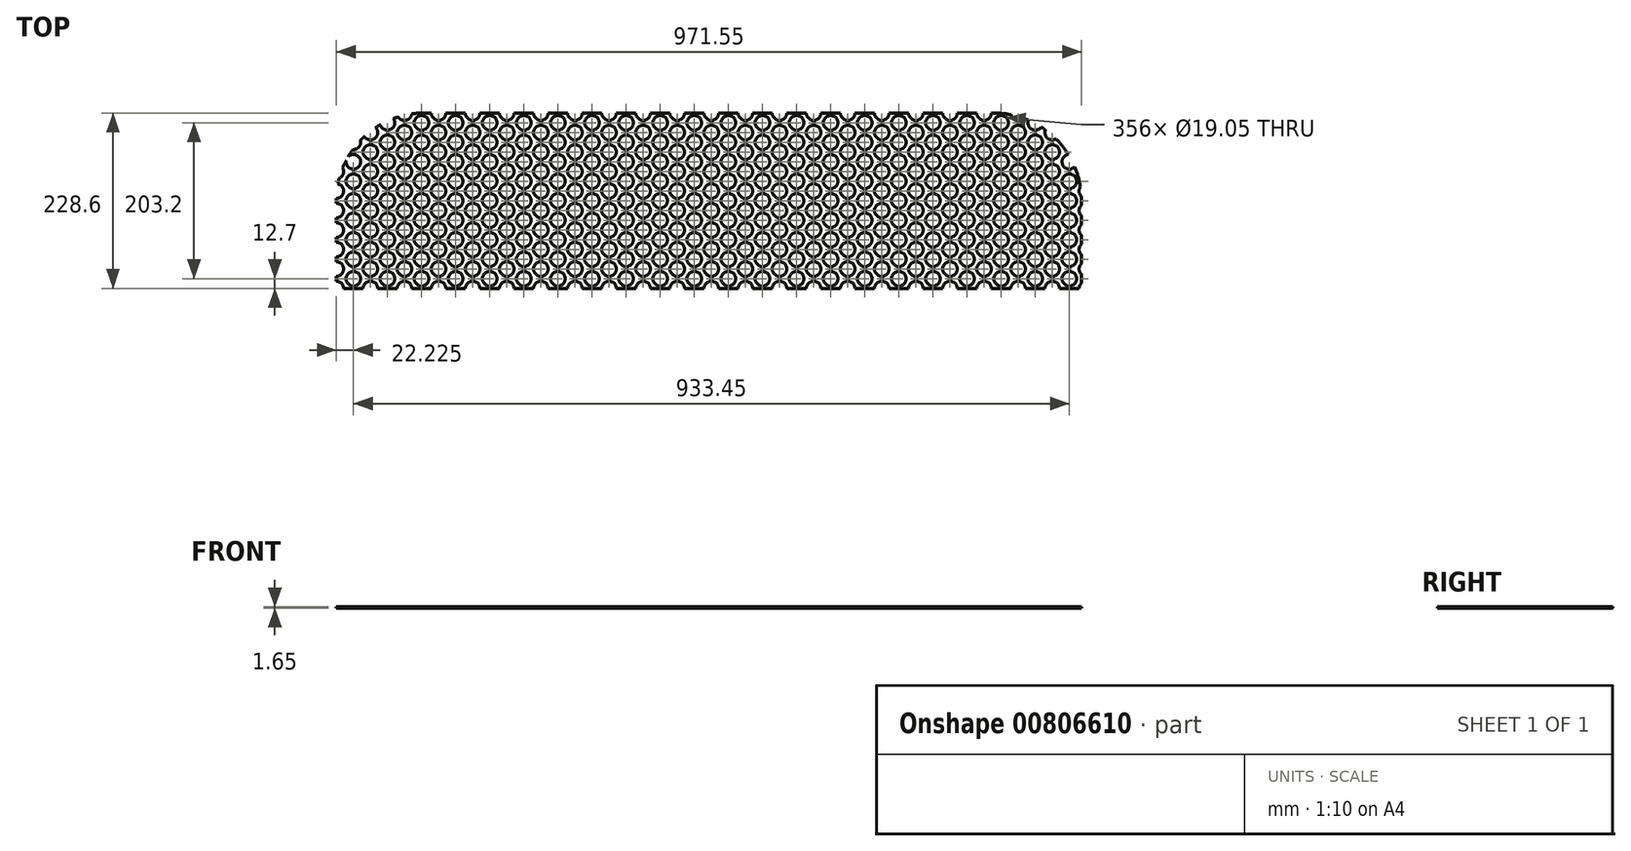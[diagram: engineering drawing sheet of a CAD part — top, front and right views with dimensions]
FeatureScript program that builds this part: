
annotation { "Feature Type Name" : "Feature", "Feature Type Description" : "" }
export const myFeature = defineFeature(function(context is Context, id is Id, definition is map)
    precondition{}
    {
        {
            var Q0;
            Q0=qCreatedBy(makeId("Top.planeOp"),FACE);
            var sketch = newSketch(context, id + "F0", { "sketchPlane" : qUnion([Q0])});
            skArc(sketch, "E0", {"start": v(9.53, 0) * mm, "mid": v(6.74, 6.74) * mm, "end": v(0, 9.53) * mm});
            skArc(sketch, "E1.0.1.0", {"start": v(0, 15.88) * mm, "mid": v(9.53, 25.4) * mm, "end": v(0, 34.92) * mm});
            skArc(sketch, "E1.0.2.0", {"start": v(0, 41.27) * mm, "mid": v(9.53, 50.8) * mm, "end": v(0, 60.32) * mm});
            skArc(sketch, "E1.0.3.0", {"start": v(0, 66.67) * mm, "mid": v(9.53, 76.2) * mm, "end": v(0, 85.72) * mm});
            skArc(sketch, "E1.0.4.0", {"start": v(0, 92.07) * mm, "mid": v(9.53, 101.6) * mm, "end": v(0, 111.12) * mm});
            skArc(sketch, "E1.0.5.0", {"start": v(0.04, 117.48) * mm, "mid": v(9.47, 125.95) * mm, "end": v(2.13, 136.28) * mm});
            skArc(sketch, "E1.0.6.0", {"start": v(3.84, 143.68) * mm, "mid": v(9.04, 149.39) * mm, "end": v(8.3, 157.07) * mm});
            skArc(sketch, "E1.1.0.0", {"start": v(53.98, 0) * mm, "mid": v(44.45, 9.53) * mm, "end": v(34.93, 0) * mm});
            skCircle(sketch, "E1.1.1.0", {"center": v(44.45, 25.4) * mm, "radius": 9.53 * mm});
            skCircle(sketch, "E1.1.2.0", {"center": v(44.45, 50.8) * mm, "radius": 9.53 * mm});
            skCircle(sketch, "E1.1.3.0", {"center": v(44.45, 76.2) * mm, "radius": 9.53 * mm});
            skCircle(sketch, "E1.1.4.0", {"center": v(44.45, 101.6) * mm, "radius": 9.53 * mm});
            skCircle(sketch, "E1.1.5.0", {"center": v(44.45, 127) * mm, "radius": 9.53 * mm});
            skCircle(sketch, "E1.1.6.0", {"center": v(44.45, 152.4) * mm, "radius": 9.53 * mm});
            skCircle(sketch, "E1.1.7.0", {"center": v(44.45, 177.8) * mm, "radius": 9.53 * mm});
            skArc(sketch, "E1.1.8.0", {"start": v(36.47, 198) * mm, "mid": v(50.33, 195.71) * mm, "end": v(51.39, 209.73) * mm});
            skArc(sketch, "E1.2.0.0", {"start": v(98.43, 0) * mm, "mid": v(88.9, 9.53) * mm, "end": v(79.38, 0) * mm});
            skCircle(sketch, "E1.2.1.0", {"center": v(88.9, 25.4) * mm, "radius": 9.53 * mm});
            skCircle(sketch, "E1.2.2.0", {"center": v(88.9, 50.8) * mm, "radius": 9.53 * mm});
            skCircle(sketch, "E1.2.3.0", {"center": v(88.9, 76.2) * mm, "radius": 9.53 * mm});
            skCircle(sketch, "E1.2.4.0", {"center": v(88.9, 101.6) * mm, "radius": 9.53 * mm});
            skCircle(sketch, "E1.2.5.0", {"center": v(88.9, 127) * mm, "radius": 9.53 * mm});
            skCircle(sketch, "E1.2.6.0", {"center": v(88.9, 152.4) * mm, "radius": 9.53 * mm});
            skCircle(sketch, "E1.2.7.0", {"center": v(88.9, 177.8) * mm, "radius": 9.53 * mm});
            skCircle(sketch, "E1.2.8.0", {"center": v(88.9, 203.2) * mm, "radius": 9.53 * mm});
            skArc(sketch, "E1.2.9.0", {"start": v(80.8, 223.58) * mm, "mid": v(90.97, 219.3) * mm, "end": v(98.36, 227.48) * mm});
            skArc(sketch, "E1.3.0.0", {"start": v(142.88, 0) * mm, "mid": v(133.35, 9.53) * mm, "end": v(123.83, 0) * mm});
            skCircle(sketch, "E1.3.1.0", {"center": v(133.35, 25.4) * mm, "radius": 9.53 * mm});
            skCircle(sketch, "E1.3.2.0", {"center": v(133.35, 50.8) * mm, "radius": 9.53 * mm});
            skCircle(sketch, "E1.3.3.0", {"center": v(133.35, 76.2) * mm, "radius": 9.53 * mm});
            skCircle(sketch, "E1.3.4.0", {"center": v(133.35, 101.6) * mm, "radius": 9.53 * mm});
            skCircle(sketch, "E1.3.5.0", {"center": v(133.35, 127) * mm, "radius": 9.53 * mm});
            skCircle(sketch, "E1.3.6.0", {"center": v(133.35, 152.4) * mm, "radius": 9.53 * mm});
            skCircle(sketch, "E1.3.7.0", {"center": v(133.35, 177.8) * mm, "radius": 9.53 * mm});
            skCircle(sketch, "E1.3.8.0", {"center": v(133.35, 203.2) * mm, "radius": 9.53 * mm});
            skArc(sketch, "E1.3.9.0", {"start": v(123.83, 228.6) * mm, "mid": v(133.35, 219.07) * mm, "end": v(142.88, 228.6) * mm});
            skArc(sketch, "E1.4.0.0", {"start": v(187.33, 0) * mm, "mid": v(177.8, 9.53) * mm, "end": v(168.28, 0) * mm});
            skCircle(sketch, "E1.4.1.0", {"center": v(177.8, 25.4) * mm, "radius": 9.53 * mm});
            skCircle(sketch, "E1.4.2.0", {"center": v(177.8, 50.8) * mm, "radius": 9.53 * mm});
            skCircle(sketch, "E1.4.3.0", {"center": v(177.8, 76.2) * mm, "radius": 9.53 * mm});
            skCircle(sketch, "E1.4.4.0", {"center": v(177.8, 101.6) * mm, "radius": 9.53 * mm});
            skCircle(sketch, "E1.4.5.0", {"center": v(177.8, 127) * mm, "radius": 9.53 * mm});
            skCircle(sketch, "E1.4.6.0", {"center": v(177.8, 152.4) * mm, "radius": 9.53 * mm});
            skCircle(sketch, "E1.4.7.0", {"center": v(177.8, 177.8) * mm, "radius": 9.53 * mm});
            skCircle(sketch, "E1.4.8.0", {"center": v(177.8, 203.2) * mm, "radius": 9.53 * mm});
            skArc(sketch, "E1.4.9.0", {"start": v(168.28, 228.6) * mm, "mid": v(177.8, 219.07) * mm, "end": v(187.33, 228.6) * mm});
            skArc(sketch, "E1.5.0.0", {"start": v(231.78, 0) * mm, "mid": v(222.25, 9.53) * mm, "end": v(212.72, 0) * mm});
            skCircle(sketch, "E1.5.1.0", {"center": v(222.25, 25.4) * mm, "radius": 9.53 * mm});
            skCircle(sketch, "E1.5.2.0", {"center": v(222.25, 50.8) * mm, "radius": 9.53 * mm});
            skCircle(sketch, "E1.5.3.0", {"center": v(222.25, 76.2) * mm, "radius": 9.53 * mm});
            skCircle(sketch, "E1.5.4.0", {"center": v(222.25, 101.6) * mm, "radius": 9.53 * mm});
            skCircle(sketch, "E1.5.5.0", {"center": v(222.25, 127) * mm, "radius": 9.53 * mm});
            skCircle(sketch, "E1.5.6.0", {"center": v(222.25, 152.4) * mm, "radius": 9.53 * mm});
            skCircle(sketch, "E1.5.7.0", {"center": v(222.25, 177.8) * mm, "radius": 9.53 * mm});
            skCircle(sketch, "E1.5.8.0", {"center": v(222.25, 203.2) * mm, "radius": 9.53 * mm});
            skArc(sketch, "E1.5.9.0", {"start": v(212.72, 228.6) * mm, "mid": v(222.25, 219.07) * mm, "end": v(231.78, 228.6) * mm});
            skArc(sketch, "E1.6.0.0", {"start": v(276.23, 0) * mm, "mid": v(266.7, 9.53) * mm, "end": v(257.18, 0) * mm});
            skCircle(sketch, "E1.6.1.0", {"center": v(266.7, 25.4) * mm, "radius": 9.53 * mm});
            skCircle(sketch, "E1.6.2.0", {"center": v(266.7, 50.8) * mm, "radius": 9.53 * mm});
            skCircle(sketch, "E1.6.3.0", {"center": v(266.7, 76.2) * mm, "radius": 9.53 * mm});
            skCircle(sketch, "E1.6.4.0", {"center": v(266.7, 101.6) * mm, "radius": 9.53 * mm});
            skCircle(sketch, "E1.6.5.0", {"center": v(266.7, 127) * mm, "radius": 9.53 * mm});
            skCircle(sketch, "E1.6.6.0", {"center": v(266.7, 152.4) * mm, "radius": 9.53 * mm});
            skCircle(sketch, "E1.6.7.0", {"center": v(266.7, 177.8) * mm, "radius": 9.53 * mm});
            skCircle(sketch, "E1.6.8.0", {"center": v(266.7, 203.2) * mm, "radius": 9.53 * mm});
            skArc(sketch, "E1.6.9.0", {"start": v(257.18, 228.6) * mm, "mid": v(266.7, 219.07) * mm, "end": v(276.23, 228.6) * mm});
            skArc(sketch, "E1.7.0.0", {"start": v(320.68, 0) * mm, "mid": v(311.15, 9.53) * mm, "end": v(301.63, 0) * mm});
            skCircle(sketch, "E1.7.1.0", {"center": v(311.15, 25.4) * mm, "radius": 9.53 * mm});
            skCircle(sketch, "E1.7.2.0", {"center": v(311.15, 50.8) * mm, "radius": 9.53 * mm});
            skCircle(sketch, "E1.7.3.0", {"center": v(311.15, 76.2) * mm, "radius": 9.53 * mm});
            skCircle(sketch, "E1.7.4.0", {"center": v(311.15, 101.6) * mm, "radius": 9.53 * mm});
            skCircle(sketch, "E1.7.5.0", {"center": v(311.15, 127) * mm, "radius": 9.53 * mm});
            skCircle(sketch, "E1.7.6.0", {"center": v(311.15, 152.4) * mm, "radius": 9.53 * mm});
            skCircle(sketch, "E1.7.7.0", {"center": v(311.15, 177.8) * mm, "radius": 9.53 * mm});
            skCircle(sketch, "E1.7.8.0", {"center": v(311.15, 203.2) * mm, "radius": 9.53 * mm});
            skArc(sketch, "E1.7.9.0", {"start": v(301.63, 228.6) * mm, "mid": v(311.15, 219.07) * mm, "end": v(320.68, 228.6) * mm});
            skArc(sketch, "E1.8.0.0", {"start": v(365.13, 0) * mm, "mid": v(355.6, 9.53) * mm, "end": v(346.08, 0) * mm});
            skCircle(sketch, "E1.8.1.0", {"center": v(355.6, 25.4) * mm, "radius": 9.53 * mm});
            skCircle(sketch, "E1.8.2.0", {"center": v(355.6, 50.8) * mm, "radius": 9.53 * mm});
            skCircle(sketch, "E1.8.3.0", {"center": v(355.6, 76.2) * mm, "radius": 9.53 * mm});
            skCircle(sketch, "E1.8.4.0", {"center": v(355.6, 101.6) * mm, "radius": 9.53 * mm});
            skCircle(sketch, "E1.8.5.0", {"center": v(355.6, 127) * mm, "radius": 9.53 * mm});
            skCircle(sketch, "E1.8.6.0", {"center": v(355.6, 152.4) * mm, "radius": 9.53 * mm});
            skCircle(sketch, "E1.8.7.0", {"center": v(355.6, 177.8) * mm, "radius": 9.53 * mm});
            skCircle(sketch, "E1.8.8.0", {"center": v(355.6, 203.2) * mm, "radius": 9.53 * mm});
            skArc(sketch, "E1.8.9.0", {"start": v(346.08, 228.6) * mm, "mid": v(355.6, 219.07) * mm, "end": v(365.13, 228.6) * mm});
            skArc(sketch, "E1.9.0.0", {"start": v(409.58, 0) * mm, "mid": v(400.05, 9.53) * mm, "end": v(390.53, 0) * mm});
            skCircle(sketch, "E1.9.1.0", {"center": v(400.05, 25.4) * mm, "radius": 9.53 * mm});
            skCircle(sketch, "E1.9.2.0", {"center": v(400.05, 50.8) * mm, "radius": 9.53 * mm});
            skCircle(sketch, "E1.9.3.0", {"center": v(400.05, 76.2) * mm, "radius": 9.53 * mm});
            skCircle(sketch, "E1.9.4.0", {"center": v(400.05, 101.6) * mm, "radius": 9.53 * mm});
            skCircle(sketch, "E1.9.5.0", {"center": v(400.05, 127) * mm, "radius": 9.53 * mm});
            skCircle(sketch, "E1.9.6.0", {"center": v(400.05, 152.4) * mm, "radius": 9.53 * mm});
            skCircle(sketch, "E1.9.7.0", {"center": v(400.05, 177.8) * mm, "radius": 9.53 * mm});
            skCircle(sketch, "E1.9.8.0", {"center": v(400.05, 203.2) * mm, "radius": 9.53 * mm});
            skArc(sketch, "E1.9.9.0", {"start": v(390.53, 228.6) * mm, "mid": v(400.05, 219.07) * mm, "end": v(409.58, 228.6) * mm});
            skArc(sketch, "E1.10.0.0", {"start": v(454.03, 0) * mm, "mid": v(444.5, 9.53) * mm, "end": v(434.98, 0) * mm});
            skCircle(sketch, "E1.10.1.0", {"center": v(444.5, 25.4) * mm, "radius": 9.53 * mm});
            skCircle(sketch, "E1.10.2.0", {"center": v(444.5, 50.8) * mm, "radius": 9.53 * mm});
            skCircle(sketch, "E1.10.3.0", {"center": v(444.5, 76.2) * mm, "radius": 9.53 * mm});
            skCircle(sketch, "E1.10.4.0", {"center": v(444.5, 101.6) * mm, "radius": 9.53 * mm});
            skCircle(sketch, "E1.10.5.0", {"center": v(444.5, 127) * mm, "radius": 9.53 * mm});
            skCircle(sketch, "E1.10.6.0", {"center": v(444.5, 152.4) * mm, "radius": 9.53 * mm});
            skCircle(sketch, "E1.10.7.0", {"center": v(444.5, 177.8) * mm, "radius": 9.53 * mm});
            skCircle(sketch, "E1.10.8.0", {"center": v(444.5, 203.2) * mm, "radius": 9.53 * mm});
            skArc(sketch, "E1.10.9.0", {"start": v(434.98, 228.6) * mm, "mid": v(444.5, 219.07) * mm, "end": v(454.03, 228.6) * mm});
            skArc(sketch, "E1.11.0.0", {"start": v(498.48, 0) * mm, "mid": v(488.95, 9.53) * mm, "end": v(479.43, 0) * mm});
            skCircle(sketch, "E1.11.1.0", {"center": v(488.95, 25.4) * mm, "radius": 9.53 * mm});
            skCircle(sketch, "E1.11.2.0", {"center": v(488.95, 50.8) * mm, "radius": 9.53 * mm});
            skCircle(sketch, "E1.11.3.0", {"center": v(488.95, 76.2) * mm, "radius": 9.53 * mm});
            skCircle(sketch, "E1.11.4.0", {"center": v(488.95, 101.6) * mm, "radius": 9.53 * mm});
            skCircle(sketch, "E1.11.5.0", {"center": v(488.95, 127) * mm, "radius": 9.53 * mm});
            skCircle(sketch, "E1.11.6.0", {"center": v(488.95, 152.4) * mm, "radius": 9.53 * mm});
            skCircle(sketch, "E1.11.7.0", {"center": v(488.95, 177.8) * mm, "radius": 9.53 * mm});
            skCircle(sketch, "E1.11.8.0", {"center": v(488.95, 203.2) * mm, "radius": 9.53 * mm});
            skArc(sketch, "E1.11.9.0", {"start": v(479.43, 228.6) * mm, "mid": v(488.95, 219.07) * mm, "end": v(498.48, 228.6) * mm});
            skArc(sketch, "E1.12.0.0", {"start": v(542.93, 0) * mm, "mid": v(533.4, 9.53) * mm, "end": v(523.88, 0) * mm});
            skCircle(sketch, "E1.12.1.0", {"center": v(533.4, 25.4) * mm, "radius": 9.53 * mm});
            skCircle(sketch, "E1.12.2.0", {"center": v(533.4, 50.8) * mm, "radius": 9.53 * mm});
            skCircle(sketch, "E1.12.3.0", {"center": v(533.4, 76.2) * mm, "radius": 9.53 * mm});
            skCircle(sketch, "E1.12.4.0", {"center": v(533.4, 101.6) * mm, "radius": 9.53 * mm});
            skCircle(sketch, "E1.12.5.0", {"center": v(533.4, 127) * mm, "radius": 9.53 * mm});
            skCircle(sketch, "E1.12.6.0", {"center": v(533.4, 152.4) * mm, "radius": 9.53 * mm});
            skCircle(sketch, "E1.12.7.0", {"center": v(533.4, 177.8) * mm, "radius": 9.53 * mm});
            skCircle(sketch, "E1.12.8.0", {"center": v(533.4, 203.2) * mm, "radius": 9.53 * mm});
            skArc(sketch, "E1.12.9.0", {"start": v(523.88, 228.6) * mm, "mid": v(533.4, 219.07) * mm, "end": v(542.93, 228.6) * mm});
            skArc(sketch, "E1.13.0.0", {"start": v(587.38, 0) * mm, "mid": v(577.85, 9.53) * mm, "end": v(568.33, 0) * mm});
            skCircle(sketch, "E1.13.1.0", {"center": v(577.85, 25.4) * mm, "radius": 9.53 * mm});
            skCircle(sketch, "E1.13.2.0", {"center": v(577.85, 50.8) * mm, "radius": 9.53 * mm});
            skCircle(sketch, "E1.13.3.0", {"center": v(577.85, 76.2) * mm, "radius": 9.53 * mm});
            skCircle(sketch, "E1.13.4.0", {"center": v(577.85, 101.6) * mm, "radius": 9.53 * mm});
            skCircle(sketch, "E1.13.5.0", {"center": v(577.85, 127) * mm, "radius": 9.53 * mm});
            skCircle(sketch, "E1.13.6.0", {"center": v(577.85, 152.4) * mm, "radius": 9.53 * mm});
            skCircle(sketch, "E1.13.7.0", {"center": v(577.85, 177.8) * mm, "radius": 9.53 * mm});
            skCircle(sketch, "E1.13.8.0", {"center": v(577.85, 203.2) * mm, "radius": 9.53 * mm});
            skArc(sketch, "E1.13.9.0", {"start": v(568.33, 228.6) * mm, "mid": v(577.85, 219.07) * mm, "end": v(587.38, 228.6) * mm});
            skArc(sketch, "E1.14.0.0", {"start": v(631.83, 0) * mm, "mid": v(622.3, 9.53) * mm, "end": v(612.78, 0) * mm});
            skCircle(sketch, "E1.14.1.0", {"center": v(622.3, 25.4) * mm, "radius": 9.53 * mm});
            skCircle(sketch, "E1.14.2.0", {"center": v(622.3, 50.8) * mm, "radius": 9.53 * mm});
            skCircle(sketch, "E1.14.3.0", {"center": v(622.3, 76.2) * mm, "radius": 9.53 * mm});
            skCircle(sketch, "E1.14.4.0", {"center": v(622.3, 101.6) * mm, "radius": 9.53 * mm});
            skCircle(sketch, "E1.14.5.0", {"center": v(622.3, 127) * mm, "radius": 9.53 * mm});
            skCircle(sketch, "E1.14.6.0", {"center": v(622.3, 152.4) * mm, "radius": 9.53 * mm});
            skCircle(sketch, "E1.14.7.0", {"center": v(622.3, 177.8) * mm, "radius": 9.53 * mm});
            skCircle(sketch, "E1.14.8.0", {"center": v(622.3, 203.2) * mm, "radius": 9.53 * mm});
            skArc(sketch, "E1.14.9.0", {"start": v(612.78, 228.6) * mm, "mid": v(622.3, 219.07) * mm, "end": v(631.83, 228.6) * mm});
            skArc(sketch, "E1.15.0.0", {"start": v(676.28, 0) * mm, "mid": v(666.75, 9.53) * mm, "end": v(657.23, 0) * mm});
            skCircle(sketch, "E1.15.1.0", {"center": v(666.75, 25.4) * mm, "radius": 9.53 * mm});
            skCircle(sketch, "E1.15.2.0", {"center": v(666.75, 50.8) * mm, "radius": 9.53 * mm});
            skCircle(sketch, "E1.15.3.0", {"center": v(666.75, 76.2) * mm, "radius": 9.53 * mm});
            skCircle(sketch, "E1.15.4.0", {"center": v(666.75, 101.6) * mm, "radius": 9.53 * mm});
            skCircle(sketch, "E1.15.5.0", {"center": v(666.75, 127) * mm, "radius": 9.53 * mm});
            skCircle(sketch, "E1.15.6.0", {"center": v(666.75, 152.4) * mm, "radius": 9.53 * mm});
            skCircle(sketch, "E1.15.7.0", {"center": v(666.75, 177.8) * mm, "radius": 9.53 * mm});
            skCircle(sketch, "E1.15.8.0", {"center": v(666.75, 203.2) * mm, "radius": 9.53 * mm});
            skArc(sketch, "E1.15.9.0", {"start": v(657.23, 228.6) * mm, "mid": v(666.75, 219.07) * mm, "end": v(676.28, 228.6) * mm});
            skArc(sketch, "E1.16.0.0", {"start": v(720.73, 0) * mm, "mid": v(711.2, 9.53) * mm, "end": v(701.68, 0) * mm});
            skCircle(sketch, "E1.16.1.0", {"center": v(711.2, 25.4) * mm, "radius": 9.53 * mm});
            skCircle(sketch, "E1.16.2.0", {"center": v(711.2, 50.8) * mm, "radius": 9.53 * mm});
            skCircle(sketch, "E1.16.3.0", {"center": v(711.2, 76.2) * mm, "radius": 9.53 * mm});
            skCircle(sketch, "E1.16.4.0", {"center": v(711.2, 101.6) * mm, "radius": 9.53 * mm});
            skCircle(sketch, "E1.16.5.0", {"center": v(711.2, 127) * mm, "radius": 9.53 * mm});
            skCircle(sketch, "E1.16.6.0", {"center": v(711.2, 152.4) * mm, "radius": 9.53 * mm});
            skCircle(sketch, "E1.16.7.0", {"center": v(711.2, 177.8) * mm, "radius": 9.53 * mm});
            skCircle(sketch, "E1.16.8.0", {"center": v(711.2, 203.2) * mm, "radius": 9.53 * mm});
            skArc(sketch, "E1.16.9.0", {"start": v(701.68, 228.6) * mm, "mid": v(711.2, 219.07) * mm, "end": v(720.73, 228.6) * mm});
            skArc(sketch, "E1.17.0.0", {"start": v(765.18, 0) * mm, "mid": v(755.65, 9.53) * mm, "end": v(746.12, 0) * mm});
            skCircle(sketch, "E1.17.1.0", {"center": v(755.65, 25.4) * mm, "radius": 9.53 * mm});
            skCircle(sketch, "E1.17.2.0", {"center": v(755.65, 50.8) * mm, "radius": 9.53 * mm});
            skCircle(sketch, "E1.17.3.0", {"center": v(755.65, 76.2) * mm, "radius": 9.53 * mm});
            skCircle(sketch, "E1.17.4.0", {"center": v(755.65, 101.6) * mm, "radius": 9.53 * mm});
            skCircle(sketch, "E1.17.5.0", {"center": v(755.65, 127) * mm, "radius": 9.53 * mm});
            skCircle(sketch, "E1.17.6.0", {"center": v(755.65, 152.4) * mm, "radius": 9.53 * mm});
            skCircle(sketch, "E1.17.7.0", {"center": v(755.65, 177.8) * mm, "radius": 9.53 * mm});
            skCircle(sketch, "E1.17.8.0", {"center": v(755.65, 203.2) * mm, "radius": 9.53 * mm});
            skArc(sketch, "E1.17.9.0", {"start": v(746.12, 228.6) * mm, "mid": v(755.65, 219.07) * mm, "end": v(765.18, 228.6) * mm});
            skArc(sketch, "E1.18.0.0", {"start": v(809.62, 0) * mm, "mid": v(800.1, 9.53) * mm, "end": v(790.58, 0) * mm});
            skCircle(sketch, "E1.18.1.0", {"center": v(800.1, 25.4) * mm, "radius": 9.53 * mm});
            skCircle(sketch, "E1.18.2.0", {"center": v(800.1, 50.8) * mm, "radius": 9.53 * mm});
            skCircle(sketch, "E1.18.3.0", {"center": v(800.1, 76.2) * mm, "radius": 9.53 * mm});
            skCircle(sketch, "E1.18.4.0", {"center": v(800.1, 101.6) * mm, "radius": 9.53 * mm});
            skCircle(sketch, "E1.18.5.0", {"center": v(800.1, 127) * mm, "radius": 9.53 * mm});
            skCircle(sketch, "E1.18.6.0", {"center": v(800.1, 152.4) * mm, "radius": 9.53 * mm});
            skCircle(sketch, "E1.18.7.0", {"center": v(800.1, 177.8) * mm, "radius": 9.53 * mm});
            skCircle(sketch, "E1.18.8.0", {"center": v(800.1, 203.2) * mm, "radius": 9.53 * mm});
            skArc(sketch, "E1.18.9.0", {"start": v(790.58, 228.6) * mm, "mid": v(800.1, 219.07) * mm, "end": v(809.62, 228.6) * mm});
            skArc(sketch, "E1.19.0.0", {"start": v(854.08, 0) * mm, "mid": v(844.55, 9.53) * mm, "end": v(835.02, 0) * mm});
            skCircle(sketch, "E1.19.1.0", {"center": v(844.55, 25.4) * mm, "radius": 9.53 * mm});
            skCircle(sketch, "E1.19.2.0", {"center": v(844.55, 50.8) * mm, "radius": 9.53 * mm});
            skCircle(sketch, "E1.19.3.0", {"center": v(844.55, 76.2) * mm, "radius": 9.53 * mm});
            skCircle(sketch, "E1.19.4.0", {"center": v(844.55, 101.6) * mm, "radius": 9.53 * mm});
            skCircle(sketch, "E1.19.5.0", {"center": v(844.55, 127) * mm, "radius": 9.53 * mm});
            skCircle(sketch, "E1.19.6.0", {"center": v(844.55, 152.4) * mm, "radius": 9.53 * mm});
            skCircle(sketch, "E1.19.7.0", {"center": v(844.55, 177.8) * mm, "radius": 9.53 * mm});
            skCircle(sketch, "E1.19.8.0", {"center": v(844.55, 203.2) * mm, "radius": 9.53 * mm});
            skArc(sketch, "E1.19.9.0", {"start": v(835.02, 228.6) * mm, "mid": v(844.55, 219.07) * mm, "end": v(854.08, 228.6) * mm});
            skArc(sketch, "E1.20.0.0", {"start": v(898.52, 0) * mm, "mid": v(889, 9.53) * mm, "end": v(879.48, 0) * mm});
            skCircle(sketch, "E1.20.1.0", {"center": v(889, 25.4) * mm, "radius": 9.53 * mm});
            skCircle(sketch, "E1.20.2.0", {"center": v(889, 50.8) * mm, "radius": 9.53 * mm});
            skCircle(sketch, "E1.20.3.0", {"center": v(889, 76.2) * mm, "radius": 9.53 * mm});
            skCircle(sketch, "E1.20.4.0", {"center": v(889, 101.6) * mm, "radius": 9.53 * mm});
            skCircle(sketch, "E1.20.5.0", {"center": v(889, 127) * mm, "radius": 9.53 * mm});
            skCircle(sketch, "E1.20.6.0", {"center": v(889, 152.4) * mm, "radius": 9.53 * mm});
            skCircle(sketch, "E1.20.7.0", {"center": v(889, 177.8) * mm, "radius": 9.53 * mm});
            skCircle(sketch, "E1.20.8.0", {"center": v(889, 203.2) * mm, "radius": 9.53 * mm});
            skArc(sketch, "E1.20.9.0", {"start": v(879.74, 226.37) * mm, "mid": v(886.45, 219.42) * mm, "end": v(895.78, 221.91) * mm});
            skArc(sketch, "E1.21.0.0", {"start": v(942.98, 0) * mm, "mid": v(933.45, 9.53) * mm, "end": v(923.93, 0) * mm});
            skCircle(sketch, "E1.21.1.0", {"center": v(933.45, 25.4) * mm, "radius": 9.53 * mm});
            skCircle(sketch, "E1.21.2.0", {"center": v(933.45, 50.8) * mm, "radius": 9.53 * mm});
            skCircle(sketch, "E1.21.3.0", {"center": v(933.45, 76.2) * mm, "radius": 9.53 * mm});
            skCircle(sketch, "E1.21.4.0", {"center": v(933.45, 101.6) * mm, "radius": 9.53 * mm});
            skCircle(sketch, "E1.21.5.0", {"center": v(933.45, 127) * mm, "radius": 9.53 * mm});
            skCircle(sketch, "E1.21.6.0", {"center": v(933.45, 152.4) * mm, "radius": 9.53 * mm});
            skCircle(sketch, "E1.21.7.0", {"center": v(933.45, 177.8) * mm, "radius": 9.53 * mm});
            skArc(sketch, "E1.21.8.0", {"start": v(924.58, 206.67) * mm, "mid": v(927.25, 195.97) * mm, "end": v(938.23, 194.96) * mm});
            skArc(sketch, "E1.22.0.0", {"start": v(971.55, 7.1) * mm, "mid": v(969.2, 3.89) * mm, "end": v(968.38, 0) * mm});
            skArc(sketch, "E1.22.1.0", {"start": v(971.55, 32.5) * mm, "mid": v(968.38, 25.4) * mm, "end": v(971.55, 18.3) * mm});
            skArc(sketch, "E1.22.2.0", {"start": v(971.55, 57.9) * mm, "mid": v(968.38, 50.8) * mm, "end": v(971.55, 43.7) * mm});
            skArc(sketch, "E1.22.3.0", {"start": v(971.55, 83.3) * mm, "mid": v(968.38, 76.2) * mm, "end": v(971.55, 69.1) * mm});
            skArc(sketch, "E1.22.4.0", {"start": v(971.55, 108.7) * mm, "mid": v(968.38, 101.6) * mm, "end": v(971.55, 94.5) * mm});
            skArc(sketch, "E1.22.5.0", {"start": v(970.1, 132.46) * mm, "mid": v(968.43, 126) * mm, "end": v(971.4, 120.03) * mm});
            skLineSegment(sketch, "E1.direction1", {"start": v(9.53, 0) * mm, "end": v(34.93, 0) * mm, "construction": true});
            skLineSegment(sketch, "E1.direction2", {"start": v(0, 9.53) * mm, "end": v(0, 15.88) * mm, "construction": true});
            skLineSegment(sketch, "E2.bottom", {"start": v(9.53, 0) * mm, "end": v(34.92, 0) * mm});
            skLineSegment(sketch, "E2.left", {"start": v(0, 9.53) * mm, "end": v(0, 25.4) * mm});
            skLineSegment(sketch, "E2.right", {"start": v(971.55, 7.1) * mm, "end": v(971.55, 18.3) * mm});
            skArc(sketch, "E3.filletArc", {"start": v(971.55, 114.3) * mm, "mid": v(971.51, 117.17) * mm, "end": v(971.4, 120.03) * mm});
            skPoint(sketch, "E4.visualSharp", {"position": v(0, 228.6) * mm});
            skArc(sketch, "E4.filletArc", {"start": v(114.3, 228.6) * mm, "mid": v(106.31, 228.32) * mm, "end": v(98.36, 227.48) * mm});
            skArc(sketch, "E5.trimOffspring", {"start": v(3.84, 143.68) * mm, "mid": v(2.93, 140) * mm, "end": v(2.13, 136.28) * mm});
            skArc(sketch, "E6.trimOffspring", {"start": v(0.04, 117.48) * mm, "mid": v(0.01, 115.89) * mm, "end": v(0, 114.3) * mm});
            skLineSegment(sketch, "E7.trimOffspring", {"start": v(0, 111.12) * mm, "end": v(0, 114.3) * mm});
            skLineSegment(sketch, "E8.trimOffspring", {"start": v(0, 85.72) * mm, "end": v(0, 92.07) * mm});
            skArc(sketch, "E9.trimOffspring", {"start": v(924.58, 206.67) * mm, "mid": v(921.84, 208.6) * mm, "end": v(919.04, 210.46) * mm});
            skArc(sketch, "E10.trimOffspring", {"start": v(879.74, 226.37) * mm, "mid": v(868.55, 228.04) * mm, "end": v(857.25, 228.6) * mm});
            skArc(sketch, "E11.trimOffspring", {"start": v(970.1, 132.46) * mm, "mid": v(967.14, 145.75) * mm, "end": v(962.62, 158.58) * mm});
            skLineSegment(sketch, "E12.trimOffspring", {"start": v(971.55, 108.7) * mm, "end": v(971.55, 114.3) * mm});
            skLineSegment(sketch, "E13.trimOffspring", {"start": v(971.55, 83.3) * mm, "end": v(971.55, 94.5) * mm});
            skLineSegment(sketch, "E14.trimOffspring", {"start": v(971.55, 57.9) * mm, "end": v(971.55, 69.1) * mm});
            skLineSegment(sketch, "E15.trimOffspring", {"start": v(971.55, 32.5) * mm, "end": v(971.55, 43.7) * mm});
            skLineSegment(sketch, "E16.trimOffspring", {"start": v(809.62, 0) * mm, "end": v(835.02, 0) * mm});
            skLineSegment(sketch, "E17.trimOffspring", {"start": v(898.52, 0) * mm, "end": v(923.93, 0) * mm});
            skLineSegment(sketch, "E18.trimOffspring", {"start": v(942.98, 0) * mm, "end": v(968.38, 0) * mm});
            skLineSegment(sketch, "E19", {"start": v(854.08, 0) * mm, "end": v(879.48, 0) * mm});
            skLineSegment(sketch, "E20.trimOffspring", {"start": v(765.18, 0) * mm, "end": v(790.58, 0) * mm});
            skLineSegment(sketch, "E21.trimOffspring", {"start": v(720.73, 0) * mm, "end": v(746.12, 0) * mm});
            skLineSegment(sketch, "E22.trimOffspring", {"start": v(676.28, 0) * mm, "end": v(701.68, 0) * mm});
            skLineSegment(sketch, "E23.trimOffspring", {"start": v(631.83, 0) * mm, "end": v(657.23, 0) * mm});
            skLineSegment(sketch, "E24.trimOffspring", {"start": v(276.23, 0) * mm, "end": v(301.63, 0) * mm});
            skLineSegment(sketch, "E25.trimOffspring", {"start": v(320.68, 0) * mm, "end": v(346.08, 0) * mm});
            skLineSegment(sketch, "E26.trimOffspring", {"start": v(365.13, 0) * mm, "end": v(390.53, 0) * mm});
            skLineSegment(sketch, "E27.trimOffspring", {"start": v(409.58, 0) * mm, "end": v(434.98, 0) * mm});
            skLineSegment(sketch, "E28.trimOffspring", {"start": v(454.03, 0) * mm, "end": v(479.43, 0) * mm});
            skLineSegment(sketch, "E29.trimOffspring", {"start": v(498.48, 0) * mm, "end": v(523.88, 0) * mm});
            skLineSegment(sketch, "E30.trimOffspring", {"start": v(542.93, 0) * mm, "end": v(568.33, 0) * mm});
            skLineSegment(sketch, "E31.trimOffspring", {"start": v(587.38, 0) * mm, "end": v(612.78, 0) * mm});
            skLineSegment(sketch, "E32", {"start": v(257.18, 0) * mm, "end": v(231.78, 0) * mm});
            skLineSegment(sketch, "E33.trimOffspring", {"start": v(187.33, 0) * mm, "end": v(212.72, 0) * mm});
            skLineSegment(sketch, "E34.trimOffspring", {"start": v(142.88, 0) * mm, "end": v(168.28, 0) * mm});
            skLineSegment(sketch, "E35.trimOffspring", {"start": v(98.42, 0) * mm, "end": v(123.83, 0) * mm});
            skCircle(sketch, "E36", {"center": v(22.22, 12.7) * mm, "radius": 9.53 * mm});
            skCircle(sketch, "E37.0.1.0", {"center": v(22.22, 38.1) * mm, "radius": 9.53 * mm});
            skCircle(sketch, "E37.0.2.0", {"center": v(22.22, 63.5) * mm, "radius": 9.53 * mm});
            skCircle(sketch, "E37.0.3.0", {"center": v(22.22, 88.9) * mm, "radius": 9.53 * mm});
            skCircle(sketch, "E37.0.4.0", {"center": v(22.22, 114.3) * mm, "radius": 9.53 * mm});
            skCircle(sketch, "E37.0.5.0", {"center": v(22.22, 139.7) * mm, "radius": 9.53 * mm});
            skArc(sketch, "E37.0.6.0", {"start": v(12.9, 167.06) * mm, "mid": v(30.56, 160.5) * mm, "end": v(15.6, 171.94) * mm});
            skArc(sketch, "E37.0.7.0", {"start": v(21.48, 181) * mm, "mid": v(29.56, 184.43) * mm, "end": v(31.41, 193) * mm});
            skCircle(sketch, "E37.1.0.0", {"center": v(66.67, 12.7) * mm, "radius": 9.53 * mm});
            skCircle(sketch, "E37.1.1.0", {"center": v(66.67, 38.1) * mm, "radius": 9.53 * mm});
            skCircle(sketch, "E37.1.2.0", {"center": v(66.67, 63.5) * mm, "radius": 9.53 * mm});
            skCircle(sketch, "E37.1.3.0", {"center": v(66.67, 88.9) * mm, "radius": 9.53 * mm});
            skCircle(sketch, "E37.1.4.0", {"center": v(66.67, 114.3) * mm, "radius": 9.53 * mm});
            skCircle(sketch, "E37.1.5.0", {"center": v(66.67, 139.7) * mm, "radius": 9.53 * mm});
            skCircle(sketch, "E37.1.6.0", {"center": v(66.67, 165.1) * mm, "radius": 9.53 * mm});
            skCircle(sketch, "E37.1.7.0", {"center": v(66.67, 190.5) * mm, "radius": 9.53 * mm});
            skCircle(sketch, "E37.2.0.0", {"center": v(111.12, 12.7) * mm, "radius": 9.53 * mm});
            skCircle(sketch, "E37.2.1.0", {"center": v(111.12, 38.1) * mm, "radius": 9.53 * mm});
            skCircle(sketch, "E37.2.2.0", {"center": v(111.12, 63.5) * mm, "radius": 9.53 * mm});
            skCircle(sketch, "E37.2.3.0", {"center": v(111.12, 88.9) * mm, "radius": 9.53 * mm});
            skCircle(sketch, "E37.2.4.0", {"center": v(111.12, 114.3) * mm, "radius": 9.53 * mm});
            skCircle(sketch, "E37.2.5.0", {"center": v(111.12, 139.7) * mm, "radius": 9.53 * mm});
            skCircle(sketch, "E37.2.6.0", {"center": v(111.12, 165.1) * mm, "radius": 9.53 * mm});
            skCircle(sketch, "E37.2.7.0", {"center": v(111.12, 190.5) * mm, "radius": 9.53 * mm});
            skCircle(sketch, "E37.3.0.0", {"center": v(155.58, 12.7) * mm, "radius": 9.53 * mm});
            skCircle(sketch, "E37.3.1.0", {"center": v(155.58, 38.1) * mm, "radius": 9.53 * mm});
            skCircle(sketch, "E37.3.2.0", {"center": v(155.58, 63.5) * mm, "radius": 9.53 * mm});
            skCircle(sketch, "E37.3.3.0", {"center": v(155.58, 88.9) * mm, "radius": 9.53 * mm});
            skCircle(sketch, "E37.3.4.0", {"center": v(155.58, 114.3) * mm, "radius": 9.53 * mm});
            skCircle(sketch, "E37.3.5.0", {"center": v(155.58, 139.7) * mm, "radius": 9.53 * mm});
            skCircle(sketch, "E37.3.6.0", {"center": v(155.58, 165.1) * mm, "radius": 9.53 * mm});
            skCircle(sketch, "E37.3.7.0", {"center": v(155.58, 190.5) * mm, "radius": 9.53 * mm});
            skCircle(sketch, "E37.4.0.0", {"center": v(200.03, 12.7) * mm, "radius": 9.53 * mm});
            skCircle(sketch, "E37.4.1.0", {"center": v(200.03, 38.1) * mm, "radius": 9.53 * mm});
            skCircle(sketch, "E37.4.2.0", {"center": v(200.03, 63.5) * mm, "radius": 9.53 * mm});
            skCircle(sketch, "E37.4.3.0", {"center": v(200.03, 88.9) * mm, "radius": 9.53 * mm});
            skCircle(sketch, "E37.4.4.0", {"center": v(200.03, 114.3) * mm, "radius": 9.53 * mm});
            skCircle(sketch, "E37.4.5.0", {"center": v(200.03, 139.7) * mm, "radius": 9.53 * mm});
            skCircle(sketch, "E37.4.6.0", {"center": v(200.03, 165.1) * mm, "radius": 9.53 * mm});
            skCircle(sketch, "E37.4.7.0", {"center": v(200.03, 190.5) * mm, "radius": 9.53 * mm});
            skCircle(sketch, "E37.5.0.0", {"center": v(244.47, 12.7) * mm, "radius": 9.53 * mm});
            skCircle(sketch, "E37.5.1.0", {"center": v(244.47, 38.1) * mm, "radius": 9.53 * mm});
            skCircle(sketch, "E37.5.2.0", {"center": v(244.47, 63.5) * mm, "radius": 9.53 * mm});
            skCircle(sketch, "E37.5.3.0", {"center": v(244.47, 88.9) * mm, "radius": 9.53 * mm});
            skCircle(sketch, "E37.5.4.0", {"center": v(244.47, 114.3) * mm, "radius": 9.53 * mm});
            skCircle(sketch, "E37.5.5.0", {"center": v(244.47, 139.7) * mm, "radius": 9.53 * mm});
            skCircle(sketch, "E37.5.6.0", {"center": v(244.47, 165.1) * mm, "radius": 9.53 * mm});
            skCircle(sketch, "E37.5.7.0", {"center": v(244.47, 190.5) * mm, "radius": 9.53 * mm});
            skCircle(sketch, "E37.6.0.0", {"center": v(288.93, 12.7) * mm, "radius": 9.53 * mm});
            skCircle(sketch, "E37.6.1.0", {"center": v(288.93, 38.1) * mm, "radius": 9.53 * mm});
            skCircle(sketch, "E37.6.2.0", {"center": v(288.93, 63.5) * mm, "radius": 9.53 * mm});
            skCircle(sketch, "E37.6.3.0", {"center": v(288.93, 88.9) * mm, "radius": 9.53 * mm});
            skCircle(sketch, "E37.6.4.0", {"center": v(288.93, 114.3) * mm, "radius": 9.53 * mm});
            skCircle(sketch, "E37.6.5.0", {"center": v(288.93, 139.7) * mm, "radius": 9.53 * mm});
            skCircle(sketch, "E37.6.6.0", {"center": v(288.93, 165.1) * mm, "radius": 9.53 * mm});
            skCircle(sketch, "E37.6.7.0", {"center": v(288.93, 190.5) * mm, "radius": 9.53 * mm});
            skCircle(sketch, "E37.7.0.0", {"center": v(333.38, 12.7) * mm, "radius": 9.53 * mm});
            skCircle(sketch, "E37.7.1.0", {"center": v(333.38, 38.1) * mm, "radius": 9.53 * mm});
            skCircle(sketch, "E37.7.2.0", {"center": v(333.38, 63.5) * mm, "radius": 9.53 * mm});
            skCircle(sketch, "E37.7.3.0", {"center": v(333.38, 88.9) * mm, "radius": 9.53 * mm});
            skCircle(sketch, "E37.7.4.0", {"center": v(333.38, 114.3) * mm, "radius": 9.53 * mm});
            skCircle(sketch, "E37.7.5.0", {"center": v(333.38, 139.7) * mm, "radius": 9.53 * mm});
            skCircle(sketch, "E37.7.6.0", {"center": v(333.38, 165.1) * mm, "radius": 9.53 * mm});
            skCircle(sketch, "E37.7.7.0", {"center": v(333.38, 190.5) * mm, "radius": 9.53 * mm});
            skCircle(sketch, "E37.8.0.0", {"center": v(377.83, 12.7) * mm, "radius": 9.53 * mm});
            skCircle(sketch, "E37.8.1.0", {"center": v(377.83, 38.1) * mm, "radius": 9.53 * mm});
            skCircle(sketch, "E37.8.2.0", {"center": v(377.83, 63.5) * mm, "radius": 9.53 * mm});
            skCircle(sketch, "E37.8.3.0", {"center": v(377.83, 88.9) * mm, "radius": 9.53 * mm});
            skCircle(sketch, "E37.8.4.0", {"center": v(377.83, 114.3) * mm, "radius": 9.53 * mm});
            skCircle(sketch, "E37.8.5.0", {"center": v(377.83, 139.7) * mm, "radius": 9.53 * mm});
            skCircle(sketch, "E37.8.6.0", {"center": v(377.83, 165.1) * mm, "radius": 9.53 * mm});
            skCircle(sketch, "E37.8.7.0", {"center": v(377.83, 190.5) * mm, "radius": 9.53 * mm});
            skCircle(sketch, "E37.9.0.0", {"center": v(422.28, 12.7) * mm, "radius": 9.53 * mm});
            skCircle(sketch, "E37.9.1.0", {"center": v(422.28, 38.1) * mm, "radius": 9.53 * mm});
            skCircle(sketch, "E37.9.2.0", {"center": v(422.28, 63.5) * mm, "radius": 9.53 * mm});
            skCircle(sketch, "E37.9.3.0", {"center": v(422.28, 88.9) * mm, "radius": 9.53 * mm});
            skCircle(sketch, "E37.9.4.0", {"center": v(422.28, 114.3) * mm, "radius": 9.53 * mm});
            skCircle(sketch, "E37.9.5.0", {"center": v(422.28, 139.7) * mm, "radius": 9.53 * mm});
            skCircle(sketch, "E37.9.6.0", {"center": v(422.28, 165.1) * mm, "radius": 9.53 * mm});
            skCircle(sketch, "E37.9.7.0", {"center": v(422.28, 190.5) * mm, "radius": 9.53 * mm});
            skCircle(sketch, "E37.10.0.0", {"center": v(466.73, 12.7) * mm, "radius": 9.53 * mm});
            skCircle(sketch, "E37.10.1.0", {"center": v(466.73, 38.1) * mm, "radius": 9.53 * mm});
            skCircle(sketch, "E37.10.2.0", {"center": v(466.73, 63.5) * mm, "radius": 9.53 * mm});
            skCircle(sketch, "E37.10.3.0", {"center": v(466.73, 88.9) * mm, "radius": 9.53 * mm});
            skCircle(sketch, "E37.10.4.0", {"center": v(466.73, 114.3) * mm, "radius": 9.53 * mm});
            skCircle(sketch, "E37.10.5.0", {"center": v(466.73, 139.7) * mm, "radius": 9.53 * mm});
            skCircle(sketch, "E37.10.6.0", {"center": v(466.73, 165.1) * mm, "radius": 9.53 * mm});
            skCircle(sketch, "E37.10.7.0", {"center": v(466.73, 190.5) * mm, "radius": 9.53 * mm});
            skCircle(sketch, "E37.11.0.0", {"center": v(511.18, 12.7) * mm, "radius": 9.53 * mm});
            skCircle(sketch, "E37.11.1.0", {"center": v(511.18, 38.1) * mm, "radius": 9.53 * mm});
            skCircle(sketch, "E37.11.2.0", {"center": v(511.18, 63.5) * mm, "radius": 9.53 * mm});
            skCircle(sketch, "E37.11.3.0", {"center": v(511.18, 88.9) * mm, "radius": 9.53 * mm});
            skCircle(sketch, "E37.11.4.0", {"center": v(511.18, 114.3) * mm, "radius": 9.53 * mm});
            skCircle(sketch, "E37.11.5.0", {"center": v(511.18, 139.7) * mm, "radius": 9.53 * mm});
            skCircle(sketch, "E37.11.6.0", {"center": v(511.18, 165.1) * mm, "radius": 9.53 * mm});
            skCircle(sketch, "E37.11.7.0", {"center": v(511.18, 190.5) * mm, "radius": 9.53 * mm});
            skCircle(sketch, "E37.12.0.0", {"center": v(555.63, 12.7) * mm, "radius": 9.53 * mm});
            skCircle(sketch, "E37.12.1.0", {"center": v(555.63, 38.1) * mm, "radius": 9.53 * mm});
            skCircle(sketch, "E37.12.2.0", {"center": v(555.63, 63.5) * mm, "radius": 9.53 * mm});
            skCircle(sketch, "E37.12.3.0", {"center": v(555.63, 88.9) * mm, "radius": 9.53 * mm});
            skCircle(sketch, "E37.12.4.0", {"center": v(555.63, 114.3) * mm, "radius": 9.53 * mm});
            skCircle(sketch, "E37.12.5.0", {"center": v(555.63, 139.7) * mm, "radius": 9.53 * mm});
            skCircle(sketch, "E37.12.6.0", {"center": v(555.63, 165.1) * mm, "radius": 9.53 * mm});
            skCircle(sketch, "E37.12.7.0", {"center": v(555.63, 190.5) * mm, "radius": 9.53 * mm});
            skCircle(sketch, "E37.13.0.0", {"center": v(600.08, 12.7) * mm, "radius": 9.53 * mm});
            skCircle(sketch, "E37.13.1.0", {"center": v(600.08, 38.1) * mm, "radius": 9.53 * mm});
            skCircle(sketch, "E37.13.2.0", {"center": v(600.08, 63.5) * mm, "radius": 9.53 * mm});
            skCircle(sketch, "E37.13.3.0", {"center": v(600.08, 88.9) * mm, "radius": 9.53 * mm});
            skCircle(sketch, "E37.13.4.0", {"center": v(600.08, 114.3) * mm, "radius": 9.53 * mm});
            skCircle(sketch, "E37.13.5.0", {"center": v(600.08, 139.7) * mm, "radius": 9.53 * mm});
            skCircle(sketch, "E37.13.6.0", {"center": v(600.08, 165.1) * mm, "radius": 9.53 * mm});
            skCircle(sketch, "E37.13.7.0", {"center": v(600.08, 190.5) * mm, "radius": 9.53 * mm});
            skCircle(sketch, "E37.14.0.0", {"center": v(644.53, 12.7) * mm, "radius": 9.53 * mm});
            skCircle(sketch, "E37.14.1.0", {"center": v(644.53, 38.1) * mm, "radius": 9.53 * mm});
            skCircle(sketch, "E37.14.2.0", {"center": v(644.53, 63.5) * mm, "radius": 9.53 * mm});
            skCircle(sketch, "E37.14.3.0", {"center": v(644.53, 88.9) * mm, "radius": 9.53 * mm});
            skCircle(sketch, "E37.14.4.0", {"center": v(644.53, 114.3) * mm, "radius": 9.53 * mm});
            skCircle(sketch, "E37.14.5.0", {"center": v(644.53, 139.7) * mm, "radius": 9.53 * mm});
            skCircle(sketch, "E37.14.6.0", {"center": v(644.53, 165.1) * mm, "radius": 9.53 * mm});
            skCircle(sketch, "E37.14.7.0", {"center": v(644.53, 190.5) * mm, "radius": 9.53 * mm});
            skCircle(sketch, "E37.15.0.0", {"center": v(688.98, 12.7) * mm, "radius": 9.53 * mm});
            skCircle(sketch, "E37.15.1.0", {"center": v(688.98, 38.1) * mm, "radius": 9.53 * mm});
            skCircle(sketch, "E37.15.2.0", {"center": v(688.98, 63.5) * mm, "radius": 9.53 * mm});
            skCircle(sketch, "E37.15.3.0", {"center": v(688.98, 88.9) * mm, "radius": 9.53 * mm});
            skCircle(sketch, "E37.15.4.0", {"center": v(688.98, 114.3) * mm, "radius": 9.53 * mm});
            skCircle(sketch, "E37.15.5.0", {"center": v(688.98, 139.7) * mm, "radius": 9.53 * mm});
            skCircle(sketch, "E37.15.6.0", {"center": v(688.98, 165.1) * mm, "radius": 9.53 * mm});
            skCircle(sketch, "E37.15.7.0", {"center": v(688.98, 190.5) * mm, "radius": 9.53 * mm});
            skCircle(sketch, "E37.16.0.0", {"center": v(733.43, 12.7) * mm, "radius": 9.53 * mm});
            skCircle(sketch, "E37.16.1.0", {"center": v(733.43, 38.1) * mm, "radius": 9.53 * mm});
            skCircle(sketch, "E37.16.2.0", {"center": v(733.43, 63.5) * mm, "radius": 9.53 * mm});
            skCircle(sketch, "E37.16.3.0", {"center": v(733.43, 88.9) * mm, "radius": 9.53 * mm});
            skCircle(sketch, "E37.16.4.0", {"center": v(733.43, 114.3) * mm, "radius": 9.53 * mm});
            skCircle(sketch, "E37.16.5.0", {"center": v(733.43, 139.7) * mm, "radius": 9.53 * mm});
            skCircle(sketch, "E37.16.6.0", {"center": v(733.43, 165.1) * mm, "radius": 9.53 * mm});
            skCircle(sketch, "E37.16.7.0", {"center": v(733.43, 190.5) * mm, "radius": 9.53 * mm});
            skCircle(sketch, "E37.17.0.0", {"center": v(777.88, 12.7) * mm, "radius": 9.53 * mm});
            skCircle(sketch, "E37.17.1.0", {"center": v(777.88, 38.1) * mm, "radius": 9.53 * mm});
            skCircle(sketch, "E37.17.2.0", {"center": v(777.88, 63.5) * mm, "radius": 9.53 * mm});
            skCircle(sketch, "E37.17.3.0", {"center": v(777.88, 88.9) * mm, "radius": 9.53 * mm});
            skCircle(sketch, "E37.17.4.0", {"center": v(777.88, 114.3) * mm, "radius": 9.53 * mm});
            skCircle(sketch, "E37.17.5.0", {"center": v(777.88, 139.7) * mm, "radius": 9.53 * mm});
            skCircle(sketch, "E37.17.6.0", {"center": v(777.88, 165.1) * mm, "radius": 9.53 * mm});
            skCircle(sketch, "E37.17.7.0", {"center": v(777.88, 190.5) * mm, "radius": 9.53 * mm});
            skCircle(sketch, "E37.18.0.0", {"center": v(822.33, 12.7) * mm, "radius": 9.53 * mm});
            skCircle(sketch, "E37.18.1.0", {"center": v(822.33, 38.1) * mm, "radius": 9.53 * mm});
            skCircle(sketch, "E37.18.2.0", {"center": v(822.33, 63.5) * mm, "radius": 9.53 * mm});
            skCircle(sketch, "E37.18.3.0", {"center": v(822.33, 88.9) * mm, "radius": 9.53 * mm});
            skCircle(sketch, "E37.18.4.0", {"center": v(822.33, 114.3) * mm, "radius": 9.53 * mm});
            skCircle(sketch, "E37.18.5.0", {"center": v(822.33, 139.7) * mm, "radius": 9.53 * mm});
            skCircle(sketch, "E37.18.6.0", {"center": v(822.33, 165.1) * mm, "radius": 9.53 * mm});
            skCircle(sketch, "E37.18.7.0", {"center": v(822.33, 190.5) * mm, "radius": 9.53 * mm});
            skCircle(sketch, "E37.19.0.0", {"center": v(866.78, 12.7) * mm, "radius": 9.53 * mm});
            skCircle(sketch, "E37.19.1.0", {"center": v(866.78, 38.1) * mm, "radius": 9.53 * mm});
            skCircle(sketch, "E37.19.2.0", {"center": v(866.78, 63.5) * mm, "radius": 9.53 * mm});
            skCircle(sketch, "E37.19.3.0", {"center": v(866.78, 88.9) * mm, "radius": 9.53 * mm});
            skCircle(sketch, "E37.19.4.0", {"center": v(866.78, 114.3) * mm, "radius": 9.53 * mm});
            skCircle(sketch, "E37.19.5.0", {"center": v(866.78, 139.7) * mm, "radius": 9.53 * mm});
            skCircle(sketch, "E37.19.6.0", {"center": v(866.78, 165.1) * mm, "radius": 9.53 * mm});
            skCircle(sketch, "E37.19.7.0", {"center": v(866.78, 190.5) * mm, "radius": 9.53 * mm});
            skCircle(sketch, "E37.20.0.0", {"center": v(911.23, 12.7) * mm, "radius": 9.53 * mm});
            skCircle(sketch, "E37.20.1.0", {"center": v(911.23, 38.1) * mm, "radius": 9.53 * mm});
            skCircle(sketch, "E37.20.2.0", {"center": v(911.23, 63.5) * mm, "radius": 9.53 * mm});
            skCircle(sketch, "E37.20.3.0", {"center": v(911.23, 88.9) * mm, "radius": 9.53 * mm});
            skCircle(sketch, "E37.20.4.0", {"center": v(911.23, 114.3) * mm, "radius": 9.53 * mm});
            skCircle(sketch, "E37.20.5.0", {"center": v(911.23, 139.7) * mm, "radius": 9.53 * mm});
            skCircle(sketch, "E37.20.6.0", {"center": v(911.23, 165.1) * mm, "radius": 9.53 * mm});
            skCircle(sketch, "E37.20.7.0", {"center": v(911.23, 190.5) * mm, "radius": 9.53 * mm});
            skCircle(sketch, "E37.21.0.0", {"center": v(955.68, 12.7) * mm, "radius": 9.53 * mm});
            skCircle(sketch, "E37.21.1.0", {"center": v(955.68, 38.1) * mm, "radius": 9.53 * mm});
            skCircle(sketch, "E37.21.2.0", {"center": v(955.68, 63.5) * mm, "radius": 9.53 * mm});
            skCircle(sketch, "E37.21.3.0", {"center": v(955.68, 88.9) * mm, "radius": 9.53 * mm});
            skCircle(sketch, "E37.21.4.0", {"center": v(955.68, 114.3) * mm, "radius": 9.53 * mm});
            skCircle(sketch, "E37.21.5.0", {"center": v(955.68, 139.7) * mm, "radius": 9.53 * mm});
            skArc(sketch, "E37.21.6.0", {"start": v(954.39, 174.54) * mm, "mid": v(947.21, 160.73) * mm, "end": v(962.62, 158.58) * mm});
            skLineSegment(sketch, "E37.direction1", {"start": v(22.22, 12.7) * mm, "end": v(66.67, 12.7) * mm, "construction": true});
            skLineSegment(sketch, "E37.direction2", {"start": v(22.22, 12.7) * mm, "end": v(22.22, 38.1) * mm, "construction": true});
            skArc(sketch, "E38.0.1.8", {"start": v(57.47, 213.47) * mm, "mid": v(70.72, 207.28) * mm, "end": v(74.44, 221.42) * mm});
            skCircle(sketch, "E38.0.2.8", {"center": v(111.12, 215.9) * mm, "radius": 9.53 * mm});
            skCircle(sketch, "E38.0.3.8", {"center": v(155.58, 215.9) * mm, "radius": 9.53 * mm});
            skCircle(sketch, "E38.0.4.8", {"center": v(200.03, 215.9) * mm, "radius": 9.53 * mm});
            skCircle(sketch, "E38.0.5.8", {"center": v(244.47, 215.9) * mm, "radius": 9.53 * mm});
            skCircle(sketch, "E38.0.6.8", {"center": v(288.93, 215.9) * mm, "radius": 9.53 * mm});
            skCircle(sketch, "E38.0.7.8", {"center": v(333.38, 215.9) * mm, "radius": 9.53 * mm});
            skCircle(sketch, "E38.0.8.8", {"center": v(377.83, 215.9) * mm, "radius": 9.53 * mm});
            skCircle(sketch, "E38.0.9.8", {"center": v(422.28, 215.9) * mm, "radius": 9.53 * mm});
            skCircle(sketch, "E38.0.10.8", {"center": v(466.73, 215.9) * mm, "radius": 9.53 * mm});
            skCircle(sketch, "E38.0.11.8", {"center": v(511.18, 215.9) * mm, "radius": 9.53 * mm});
            skCircle(sketch, "E38.0.12.8", {"center": v(555.63, 215.9) * mm, "radius": 9.53 * mm});
            skCircle(sketch, "E38.0.13.8", {"center": v(600.08, 215.9) * mm, "radius": 9.53 * mm});
            skCircle(sketch, "E38.0.14.8", {"center": v(644.53, 215.9) * mm, "radius": 9.53 * mm});
            skCircle(sketch, "E38.0.15.8", {"center": v(688.98, 215.9) * mm, "radius": 9.53 * mm});
            skCircle(sketch, "E38.0.16.8", {"center": v(733.43, 215.9) * mm, "radius": 9.53 * mm});
            skCircle(sketch, "E38.0.17.8", {"center": v(777.88, 215.9) * mm, "radius": 9.53 * mm});
            skCircle(sketch, "E38.0.18.8", {"center": v(822.33, 215.9) * mm, "radius": 9.53 * mm});
            skCircle(sketch, "E38.0.19.8", {"center": v(866.78, 215.9) * mm, "radius": 9.53 * mm});
            skArc(sketch, "E38.0.20.8", {"start": v(902.34, 219.33) * mm, "mid": v(906.76, 207.49) * mm, "end": v(919.04, 210.46) * mm});
            skLineSegment(sketch, "E39.trimOffspring", {"start": v(53.97, 0) * mm, "end": v(79.37, 0) * mm});
            skLineSegment(sketch, "E40.trimOffspring", {"start": v(0, 34.92) * mm, "end": v(0, 41.28) * mm});
            skLineSegment(sketch, "E41.trimOffspring", {"start": v(0, 60.32) * mm, "end": v(0, 66.67) * mm});
            skArc(sketch, "E42.trimOffspring", {"start": v(12.9, 167.06) * mm, "mid": v(10.48, 162.12) * mm, "end": v(8.3, 157.07) * mm});
            skArc(sketch, "E43.trimOffspring", {"start": v(21.48, 181) * mm, "mid": v(18.43, 176.54) * mm, "end": v(15.6, 171.94) * mm});
            skArc(sketch, "E44.trimOffspring", {"start": v(36.47, 198) * mm, "mid": v(33.9, 195.54) * mm, "end": v(31.41, 193) * mm});
            skArc(sketch, "E45.trimOffspring", {"start": v(57.47, 213.47) * mm, "mid": v(54.4, 211.65) * mm, "end": v(51.39, 209.73) * mm});
            skArc(sketch, "E46.trimOffspring", {"start": v(80.8, 223.58) * mm, "mid": v(77.6, 222.55) * mm, "end": v(74.44, 221.42) * mm});
            skLineSegment(sketch, "E47.trimOffspring", {"start": v(142.88, 228.6) * mm, "end": v(168.28, 228.6) * mm});
            skLineSegment(sketch, "E48", {"start": v(123.83, 228.6) * mm, "end": v(114.3, 228.6) * mm});
            skLineSegment(sketch, "E49.trimOffspring", {"start": v(320.68, 228.6) * mm, "end": v(346.08, 228.6) * mm});
            skLineSegment(sketch, "E50.trimOffspring", {"start": v(276.23, 228.6) * mm, "end": v(301.63, 228.6) * mm});
            skLineSegment(sketch, "E51.trimOffspring", {"start": v(187.33, 228.6) * mm, "end": v(212.72, 228.6) * mm});
            skLineSegment(sketch, "E52.trimOffspring", {"start": v(231.78, 228.6) * mm, "end": v(257.18, 228.6) * mm});
            skLineSegment(sketch, "E53.trimOffspring", {"start": v(365.13, 228.6) * mm, "end": v(390.53, 228.6) * mm});
            skArc(sketch, "E54.trimOffspring", {"start": v(954.39, 174.54) * mm, "mid": v(946.9, 185.21) * mm, "end": v(938.23, 194.96) * mm});
            skLineSegment(sketch, "E55.trimOffspring", {"start": v(720.73, 228.6) * mm, "end": v(746.12, 228.6) * mm});
            skLineSegment(sketch, "E56.trimOffspring", {"start": v(765.18, 228.6) * mm, "end": v(790.58, 228.6) * mm});
            skLineSegment(sketch, "E57.trimOffspring", {"start": v(809.62, 228.6) * mm, "end": v(835.02, 228.6) * mm});
            skLineSegment(sketch, "E58.trimOffspring", {"start": v(854.08, 228.6) * mm, "end": v(857.25, 228.6) * mm});
            skArc(sketch, "E59.trimOffspring", {"start": v(902.34, 219.33) * mm, "mid": v(899.08, 220.67) * mm, "end": v(895.78, 221.91) * mm});
            skLineSegment(sketch, "E60.trimOffspring", {"start": v(587.38, 228.6) * mm, "end": v(612.78, 228.6) * mm});
            skLineSegment(sketch, "E61.trimOffspring", {"start": v(631.83, 228.6) * mm, "end": v(657.23, 228.6) * mm});
            skLineSegment(sketch, "E62.trimOffspring", {"start": v(676.28, 228.6) * mm, "end": v(701.68, 228.6) * mm});
            skLineSegment(sketch, "E63.trimOffspring", {"start": v(409.58, 228.6) * mm, "end": v(434.98, 228.6) * mm});
            skLineSegment(sketch, "E64.trimOffspring", {"start": v(454.03, 228.6) * mm, "end": v(479.43, 228.6) * mm});
            skLineSegment(sketch, "E65.trimOffspring", {"start": v(498.48, 228.6) * mm, "end": v(523.88, 228.6) * mm});
            skLineSegment(sketch, "E66.trimOffspring", {"start": v(542.93, 228.6) * mm, "end": v(568.33, 228.6) * mm});
            skSolve(sketch);
        }
        {
            var Q0;
            {var subQ1=sQuery(id+"F0.wireOp",EDGE,"E0");Q0=makeQuery(id+"F0.imprint","IMPRINT",FACE,{"disambiguationData":[TD([[makeQuery(id+"F0.imprint","IMPRINT",EDGE,{"derivedFrom":subQ1}),-1.0]])]});}
            extrude(context, id + "F1", {"entities" : qUnion([Q0]), "depth" : 1.65 * mm, "offsetDistance" : 25.4 * mm});
        }
    });
